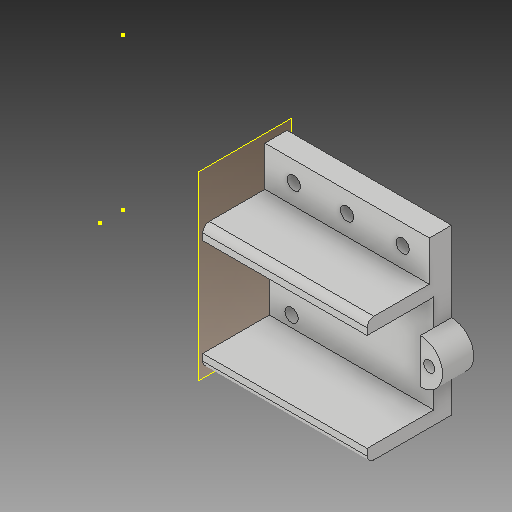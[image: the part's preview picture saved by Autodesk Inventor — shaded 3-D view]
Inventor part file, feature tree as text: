
AUTODESK INVENTOR PART (.ipt)
format: ipt  version: 2019 (Build 230136000, 136)  size: 355,328 bytes
history: native  units: mm
features: sketch x9, extrude x6, other x5, fillet x2, mirror x1, projected_geometry x1
ambient origin geometry x8: Origin, YZ Plane, XZ Plane, XY Plane, X Axis, Y Axis, Z Axis, Center Point
bodies: Body1 (feature_tree), Body2 (feature_tree)
feature tree (24):
  other  "Bryła1"
  sketch  "Szkic1"
  extrude  "Wyciągnięcie proste1"  Depth=37.0mm
  extrude  "Wyciągnięcie proste2"  Depth=22.0mm
  extrude  "Wyciągnięcie proste3"  Depth=5.0mm
  extrude  "Wyciągnięcie proste4"  Depth=2.5mm
  fillet  "Zaokrąglenie2"  Radius=3.0mm
  fillet  "Zaokrąglenie3"  Radius=3.0mm
  extrude  "Wyciągnięcie proste5"  Depth=37.0mm
  extrude  "Wyciągnięcie proste6"  Depth=3.0mm
  mirror  "Odbij1"
  other  "Płaszczyzna konstrukcyjna1"
  other  "Podział1"
  sketch  "Szkic5"
  sketch  "Szkic6"
  sketch  "Szkic7"
  sketch  "Szkic8"
  sketch  "Szkic9"
  sketch  "Szkic2"
  sketch  "Szkic3"
  projected_geometry  "Pętla rzutowana1"
  sketch  "Szkic4"
  other  "Szyk z Bryła1:1"
  other  "Bryła2"
